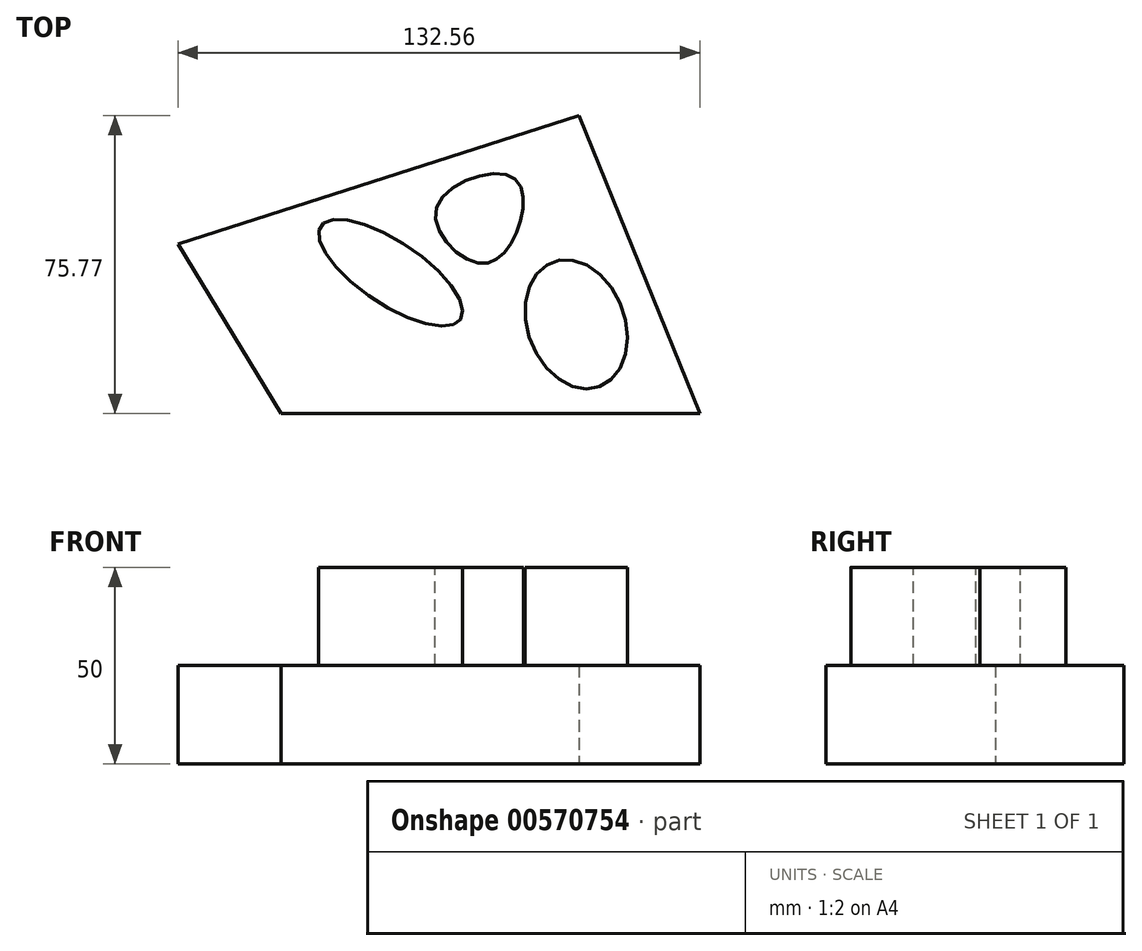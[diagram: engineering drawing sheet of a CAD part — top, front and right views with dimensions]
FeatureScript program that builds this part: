
annotation { "Feature Type Name" : "Feature", "Feature Type Description" : "" }
export const myFeature = defineFeature(function(context is Context, id is Id, definition is map)
    precondition{}
    {
        {
            var Q0;
            Q0=qCreatedBy(makeId("Top.planeOp"),FACE);
            var sketch = newSketch(context, id + "F0", { "sketchPlane" : qUnion([Q0])});
            skLineSegment(sketch, "E0", {"start": v(0, 0) * mm, "end": v(106.35, 0) * mm});
            skLineSegment(sketch, "E1", {"start": v(106.35, 0) * mm, "end": v(75.64, 75.77) * mm});
            skLineSegment(sketch, "E2", {"start": v(75.64, 75.77) * mm, "end": v(-26.21, 43.06) * mm});
            skLineSegment(sketch, "E3", {"start": v(-26.21, 43.06) * mm, "end": v(0, 0) * mm});
            skSolve(sketch);
        }
        {
            var Q0;
            Q0 = qSketchRegion(id + "F0", true);
            extrude(context, id + "F1", {"entities" : qUnion([Q0]), "depth" : 25 * mm, "offsetDistance" : 25 * mm});
        }
        {
            var Q0;
            Q0=makeQuery(id+"F1.opExtrude","CAP_FACE",FACE,{"disambiguationData":[OSD([sQuery(id+"F0.wireOp",EDGE,"E0"),sQuery(id+"F0.wireOp",EDGE,"E1"),sQuery(id+"F0.wireOp",EDGE,"E2"),sQuery(id+"F0.wireOp",EDGE,"E3")])],"isStart":false});
            var sketch = newSketch(context, id + "F2", { "sketchPlane" : qUnion([Q0])});
            skEllipse(sketch, "E4", {"center": v(27.77, 35.82) * mm, "majorRadius": 21.37 * mm, "minorRadius": 7.98 * mm, "majorAxis": v(0.83, -0.55)});
            skEllipse(sketch, "E5", {"center": v(74.95, 22.73) * mm, "majorRadius": 16.88 * mm, "minorRadius": 12.36 * mm, "majorAxis": v(0.35, -0.94)});
            skFitSpline(sketch, "E6", {"points": [v(39.38, 52.37) * mm, v(58.4, 60.27) * mm, v(59.88, 46.44) * mm, v(50, 38.3) * mm, v(39.38, 52.37) * mm]});
            skSolve(sketch);
        }
        {
            var Q0;
            Q0 = qSketchRegion(id + "F2", true);
            extrude(context, id + "F3", {"entities" : qUnion([Q0]), "operationType" : NewBodyOperationType.ADD, "depth" : 25 * mm, "offsetDistance" : 25 * mm, "hasSecondDirection" : true, "secondDirectionOppositeDirection" : true, "secondDirectionDepth" : 25 * mm});
        }
    });
